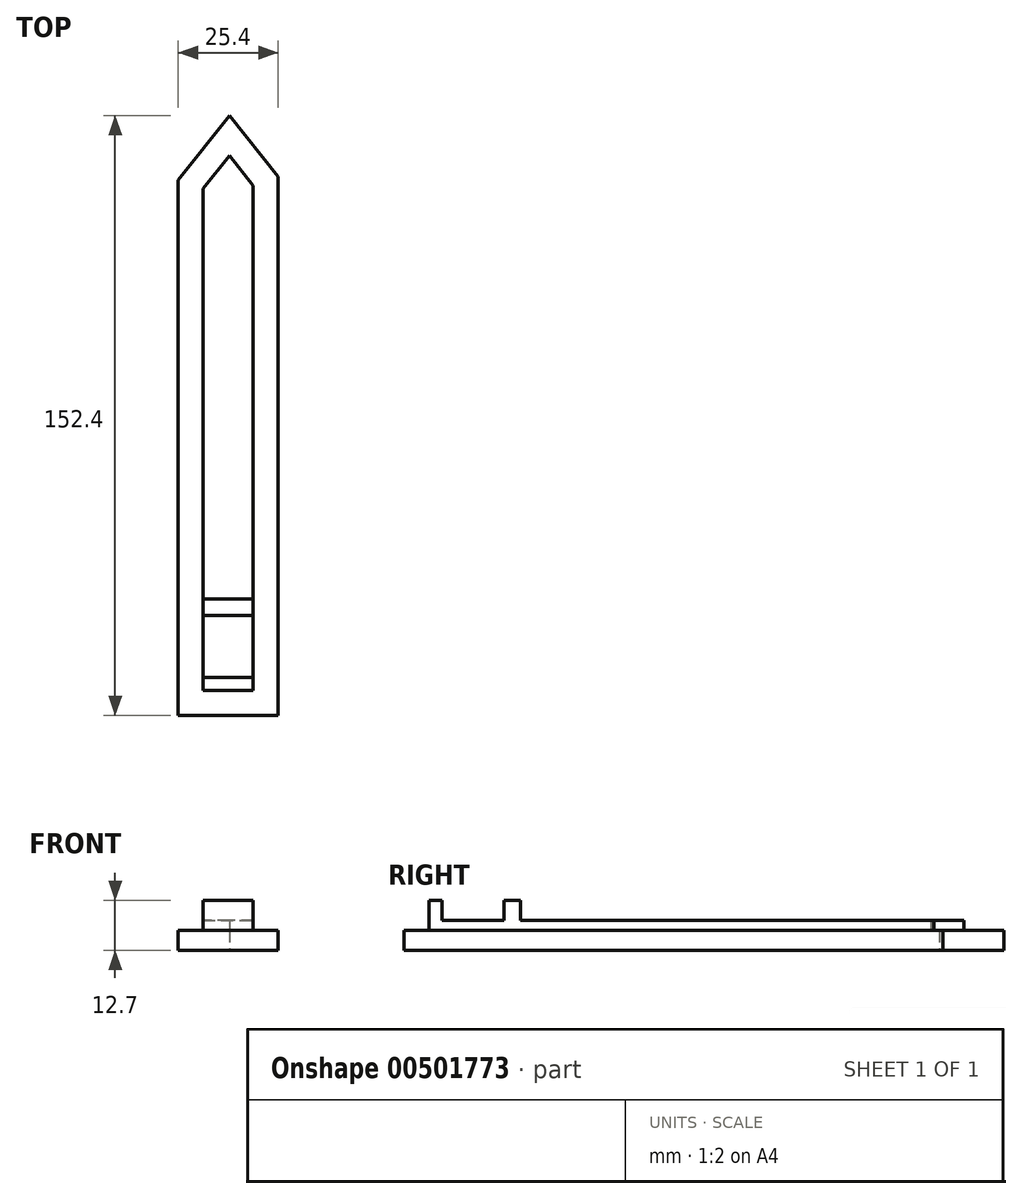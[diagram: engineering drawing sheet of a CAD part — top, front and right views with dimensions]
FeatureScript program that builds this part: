
annotation { "Feature Type Name" : "Feature", "Feature Type Description" : "" }
export const myFeature = defineFeature(function(context is Context, id is Id, definition is map)
    precondition{}
    {
        {
            var Q0;
            Q0=qCreatedBy(makeId("Top.planeOp"),FACE);
            var sketch = newSketch(context, id + "F0", { "sketchPlane" : qUnion([Q0])});
            skLineSegment(sketch, "E0.top", {"start": v(-36.6, -82.9) * mm, "end": v(-11.2, -82.9) * mm});
            skLineSegment(sketch, "E1", {"start": v(-23.58, 69.5) * mm, "end": v(-36.6, 53.15) * mm});
            skLineSegment(sketch, "E2", {"start": v(-11.2, 53.95) * mm, "end": v(-23.58, 69.5) * mm});
            skLineSegment(sketch, "E3", {"start": v(-36.6, 53.15) * mm, "end": v(-36.6, -82.9) * mm});
            skLineSegment(sketch, "E4", {"start": v(-11.2, -82.9) * mm, "end": v(-11.2, 53.95) * mm});
            skLineSegment(sketch, "E5.0", {"start": v(-30.25, -76.54) * mm, "end": v(-17.55, -76.54) * mm});
            skLineSegment(sketch, "E5.1", {"start": v(-30.25, 50.93) * mm, "end": v(-30.25, -76.54) * mm});
            skLineSegment(sketch, "E5.2", {"start": v(-17.55, -76.54) * mm, "end": v(-17.55, 51.73) * mm});
            skLineSegment(sketch, "E5.3", {"start": v(-17.55, 51.73) * mm, "end": v(-23.58, 59.3) * mm});
            skLineSegment(sketch, "E5.4", {"start": v(-23.58, 59.3) * mm, "end": v(-30.25, 50.93) * mm});
            skLineSegment(sketch, "E6.left", {"start": v(-30.25, -16) * mm, "end": v(-30.25, -19.87) * mm});
            skLineSegment(sketch, "E6.right", {"start": v(-17.55, -16) * mm, "end": v(-17.55, -19.87) * mm});
            skLineSegment(sketch, "E7.bottom", {"start": v(-30.25, -57.5) * mm, "end": v(-17.55, -57.5) * mm});
            skLineSegment(sketch, "E7.top", {"start": v(-30.25, -53.34) * mm, "end": v(-17.55, -53.34) * mm});
            skLineSegment(sketch, "E7.left", {"start": v(-30.25, -57.5) * mm, "end": v(-30.25, -53.34) * mm});
            skLineSegment(sketch, "E7.right", {"start": v(-17.55, -57.5) * mm, "end": v(-17.55, -53.34) * mm});
            skLineSegment(sketch, "E8.bottom", {"start": v(-36.6, -73.24) * mm, "end": v(-11.2, -73.24) * mm});
            skLineSegment(sketch, "E8.top", {"start": v(-36.6, -79.42) * mm, "end": v(-11.2, -79.42) * mm});
            skLineSegment(sketch, "E8.left", {"start": v(-36.6, -73.24) * mm, "end": v(-36.6, -79.42) * mm});
            skLineSegment(sketch, "E8.right", {"start": v(-11.2, -73.24) * mm, "end": v(-11.2, -79.42) * mm});
            skSolve(sketch);
        }
        {
            var Q0;
            {var subQ11=sQuery(id+"F0.wireOp",EDGE,"E1");Q0=makeQuery(id+"F0.imprint","IMPRINT",FACE,{"disambiguationData":[TD([[makeQuery(id+"F0.imprint","IMPRINT",EDGE,{"derivedFrom":subQ11}),1.0]])]});}
            var Q1;
            {var subQ4=sQuery(id+"F0.wireOp",EDGE,"E5.0");Q1=makeQuery(id+"F0.imprint","IMPRINT",FACE,{"disambiguationData":[TD([[makeQuery(id+"F0.imprint","IMPRINT",EDGE,{"derivedFrom":subQ4}),-1.0]])]});}
            var Q2;
            {var subQ0=sQuery(id+"F0.wireOp",EDGE,"E0.top");Q2=makeQuery(id+"F0.imprint","IMPRINT",FACE,{"disambiguationData":[TD([[makeQuery(id+"F0.imprint","IMPRINT",EDGE,{"derivedFrom":subQ0}),1.0]])]});}
            extrude(context, id + "F1", {"entities" : qUnion([Q0, Q1, Q2]), "depth" : 5.08 * mm});
        }
        {
            var Q0;
            {var subQ0=sQuery(id+"F0.wireOp",EDGE,"E7.bottom");Q0=makeQuery(id+"F0.imprint","IMPRINT",FACE,{"disambiguationData":[TD([[makeQuery(id+"F0.imprint","IMPRINT",EDGE,{"derivedFrom":subQ0}),-1.0]])]});}
            var Q1;
            {var subQ0=sQuery(id+"F0.wireOp",EDGE,"E5.3");Q1=makeQuery(id+"F0.imprint","IMPRINT",FACE,{"disambiguationData":[TD([[makeQuery(id+"F0.imprint","IMPRINT",EDGE,{"derivedFrom":subQ0}),1.0]])]});}
            extrude(context, id + "F2", {"entities" : qUnion([Q0, Q1]), "operationType" : NewBodyOperationType.ADD, "depth" : 7.62 * mm});
        }
        {
            var Q0;
            Q0=makeQuery(id+"F0.imprint","IMPRINT",FACE,{"disambiguationData":[TD([[makeQuery(id+"F0.imprint","IMPRINT",EDGE,{"derivedFrom":sQuery(id+"F0.wireOp",EDGE,"E7.bottom")}),1.0]])]});
            var Q1;
            {var subQ0=sQuery(id+"F0.wireOp",EDGE,"E5.0");Q1=makeQuery(id+"F0.imprint","IMPRINT",FACE,{"disambiguationData":[TD([[makeQuery(id+"F0.imprint","IMPRINT",EDGE,{"derivedFrom":subQ0}),1.0]])]});}
            extrude(context, id + "F3", {"entities" : qUnion([Q0, Q1]), "operationType" : NewBodyOperationType.ADD, "depth" : 12.7 * mm});
        }
    });
